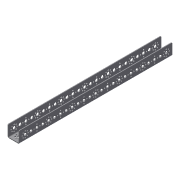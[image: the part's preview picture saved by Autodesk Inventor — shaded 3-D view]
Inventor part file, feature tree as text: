
AUTODESK INVENTOR PART (.ipt)
format: ipt  version: 2013 (Build 170138000, 138)  size: 530,432 bytes
history: native  units: mm
features: hole x28, other x5, sheet_metal_op x4, sketch x3, extrude x1, fillet x1
ambient origin geometry x8: Origin, YZ Plane, XZ Plane, XY Plane, X Axis, Y Axis, Z Axis, Center Point
bodies: Solid1 (feature_tree)
feature tree (42):
  other  "Blocks"
  sheet_metal_op  "Face1"
  sheet_metal_op  "Flange1"
  extrude  "Extrusion1"  Depth=416.0mm
  fillet  "Fillet1"  Radius=16.0mm
  sketch  "Sketch1"  dims[d0=32.0mm d1=416.0mm d3=16.0mm d4=3.7mm]
  hole  "Hole Pattern 4"  [1 undecoded]
  hole  "Hole Pattern 8"  [1 undecoded]
  other  "Plate1"
  sketch  "Sketch2"  dims[d6=16.0mm d8=16.0mm]
  other  "Plate2"
  sheet_metal_op  "Bend1"
  sheet_metal_op  "Corner1"
  sketch  "Sketch3"  dims[d9=16.0mm d10=8.0mm d13=3.7mm d14=8.0mm d15=80.0mm d17=360.0deg d20=16.0mm d21=16.0mm d22=16.0mm d23=16.0mm d25=16.0mm d26=16.0mm d27=2.0mm d28=2.0mm d29=1.0mm d30=4.0mm d31=2.0mm d32=32.0mm d33=90.0deg d34=2.0mm d35=8.0mm d36=2.0mm d37=2.0mm d38=16.0mm d39=16.0mm d40=16.0mm d41=16.0mm d42=16.0mm d43=16.0mm d45=16.0mm d46=10.0mm d47=0.0mm d48=2.0mm]
  other  "416 mm hole pattern"
  hole  "Hole Pattern 4:1"  [1 undecoded]
  hole  "Hole Pattern 8:1"  [1 undecoded]
  hole  "Hole Pattern 8:2"  [1 undecoded]
  hole  "Hole Pattern 4:2"  [1 undecoded]
  hole  "Hole Pattern 8:3"  [1 undecoded]
  hole  "Hole Pattern 4:3"  [1 undecoded]
  hole  "Hole Pattern 8:4"  [1 undecoded]
  hole  "Hole Pattern 4:4"  [1 undecoded]
  hole  "Hole Pattern 8:5"  [1 undecoded]
  hole  "Hole Pattern 8:6"  [1 undecoded]
  hole  "Hole Pattern 4:5"  [1 undecoded]
  hole  "Hole Pattern 8:7"  [1 undecoded]
  hole  "Hole Pattern 4:6"  [1 undecoded]
  other  "416 mm hole pattern:1"
  hole  "Hole Pattern 4:13"  [1 undecoded]
  hole  "Hole Pattern 8:15"  [1 undecoded]
  hole  "Hole Pattern 8:16"  [1 undecoded]
  hole  "Hole Pattern 4:14"  [1 undecoded]
  hole  "Hole Pattern 8:17"  [1 undecoded]
  hole  "Hole Pattern 4:15"  [1 undecoded]
  hole  "Hole Pattern 8:18"  [1 undecoded]
  hole  "Hole Pattern 4:16"  [1 undecoded]
  hole  "Hole Pattern 8:19"  [1 undecoded]
  hole  "Hole Pattern 8:20"  [1 undecoded]
  hole  "Hole Pattern 4:17"  [1 undecoded]
  hole  "Hole Pattern 8:21"  [1 undecoded]
  hole  "Hole Pattern 4:18"  [1 undecoded]
note: 28 required parameter values undecoded (feature->parameter linkage not recoverable at this tier; creation-order binding heuristic only, values carry confidence <= 0.55)
